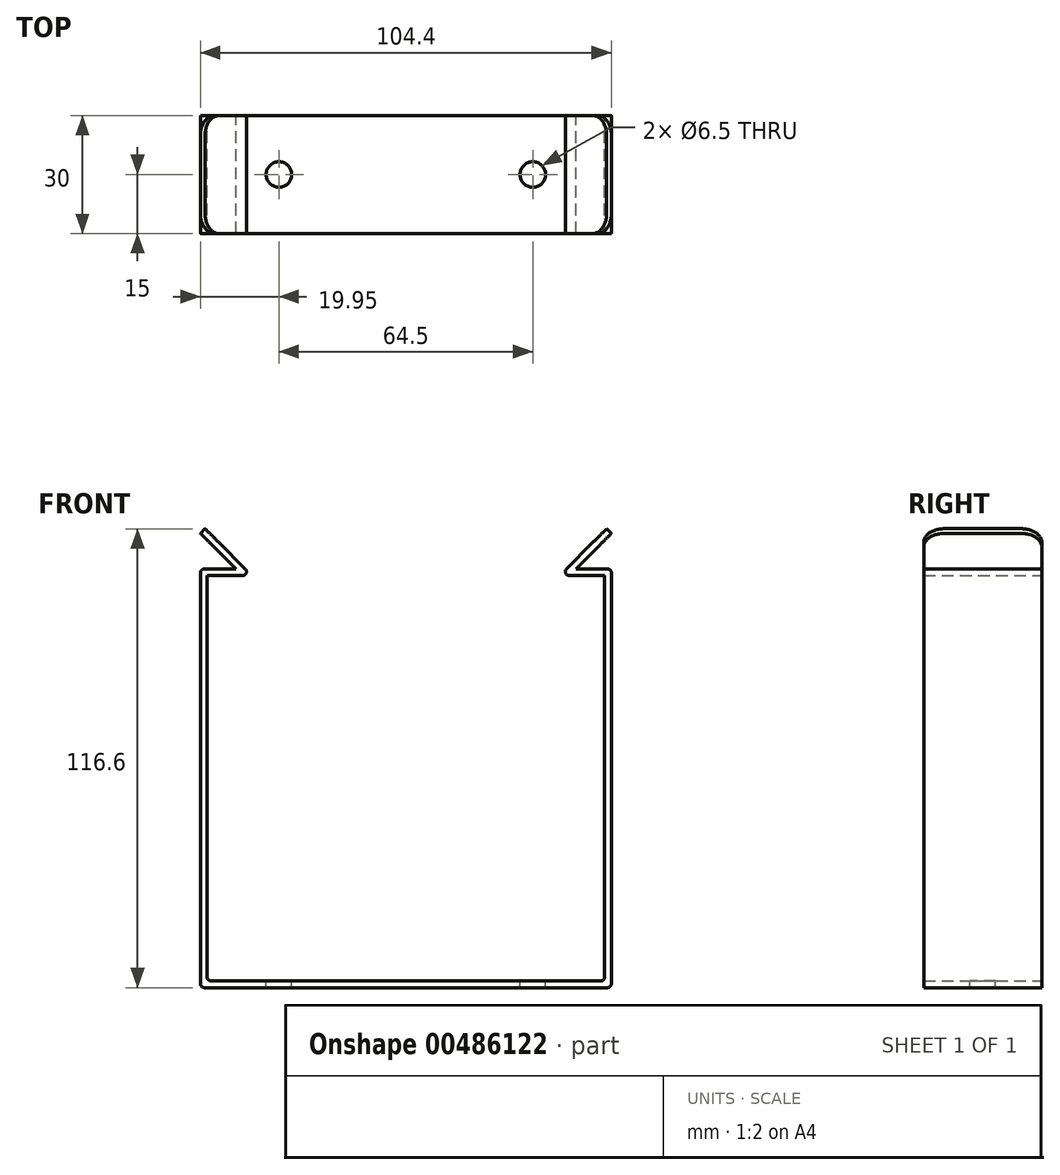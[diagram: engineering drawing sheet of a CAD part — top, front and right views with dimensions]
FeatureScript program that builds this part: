
annotation { "Feature Type Name" : "Feature", "Feature Type Description" : "" }
export const myFeature = defineFeature(function(context is Context, id is Id, definition is map)
    precondition{}
    {
        {
            var Q0;
            Q0=qCreatedBy(makeId("Front.planeOp"),FACE);
            var sketch = newSketch(context, id + "F0", { "sketchPlane" : qUnion([Q0])});
            skLineSegment(sketch, "E0", {"start": v(0, 0) * mm, "end": v(50.5, 0) * mm});
            skLineSegment(sketch, "E1", {"start": v(50.5, 0) * mm, "end": v(50.5, 103) * mm});
            skLineSegment(sketch, "E2", {"start": v(50.5, 103) * mm, "end": v(41.29, 103) * mm});
            skLineSegment(sketch, "E3", {"start": v(0, -1.7) * mm, "end": v(52.2, -1.7) * mm});
            skLineSegment(sketch, "E4", {"start": v(52.2, -1.7) * mm, "end": v(52.2, 104.7) * mm});
            skLineSegment(sketch, "E5", {"start": v(52.2, 104.7) * mm, "end": v(43.2, 104.7) * mm});
            skLineSegment(sketch, "E6", {"start": v(43.2, 104.7) * mm, "end": v(52.2, 113.7) * mm});
            skLineSegment(sketch, "E7", {"start": v(52.2, 113.7) * mm, "end": v(51, 114.9) * mm});
            skLineSegment(sketch, "E8", {"start": v(51, 114.9) * mm, "end": v(39.1, 103) * mm});
            skLineSegment(sketch, "E9", {"start": v(39.1, 103) * mm, "end": v(41.29, 103) * mm});
            skLineSegment(sketch, "E10.MirrorCS", {"start": v(-52.2, 113.7) * mm, "end": v(-51, 114.9) * mm});
            skLineSegment(sketch, "E11.MirrorCS", {"start": v(-39.1, 103) * mm, "end": v(-41.29, 103) * mm});
            skLineSegment(sketch, "E12.MirrorCS", {"start": v(-50.5, 103) * mm, "end": v(-41.29, 103) * mm});
            skLineSegment(sketch, "E13.MirrorCS", {"start": v(-43.2, 104.7) * mm, "end": v(-52.2, 113.7) * mm});
            skLineSegment(sketch, "E14.MirrorCS", {"start": v(-52.2, 104.7) * mm, "end": v(-43.2, 104.7) * mm});
            skLineSegment(sketch, "E15.MirrorCS", {"start": v(-51, 114.9) * mm, "end": v(-39.1, 103) * mm});
            skLineSegment(sketch, "E16.MirrorCS", {"start": v(0, 0) * mm, "end": v(-50.5, 0) * mm});
            skLineSegment(sketch, "E17.MirrorCS", {"start": v(-50.5, 0) * mm, "end": v(-50.5, 103) * mm});
            skLineSegment(sketch, "E18.MirrorCS", {"start": v(0, -1.7) * mm, "end": v(-52.2, -1.7) * mm});
            skLineSegment(sketch, "E19.MirrorCS", {"start": v(-52.2, -1.7) * mm, "end": v(-52.2, 104.7) * mm});
            skSolve(sketch);
        }
        {
            var Q0;
            Q0=makeQuery(id+"F0.imprint","IMPRINT",FACE,{"disambiguationData":[TD([[makeQuery(id+"F0.imprint","IMPRINT",EDGE,{"derivedFrom":sQuery(id+"F0.wireOp",EDGE,"E0")}),-1.0]])]});
            extrude(context, id + "F1", {"entities" : qUnion([Q0]), "depth" : 30 * mm});
        }
        {
            var Q0;
            Q0=makeQuery(id+"F1.opExtrude","SWEPT_FACE",FACE,{"disambiguationData":[OSD([sQuery(id+"F0.wireOp",EDGE,"E0"),sQuery(id+"F0.wireOp",EDGE,"E16.MirrorCS")])]});
            var sketch = newSketch(context, id + "F2", { "sketchPlane" : qUnion([Q0])});
            skCircle(sketch, "E20", {"center": v(-32.25, -15) * mm, "radius": 3.25 * mm});
            skCircle(sketch, "E21.MirrorC", {"center": v(32.25, -15) * mm, "radius": 3.25 * mm});
            skSolve(sketch);
        }
        {
            var Q0;
            Q0=sQuery(id+"F2.wireOp",VERTEX,"E21.MirrorC.center");
            var Q1;
            Q1=sQuery(id+"F2.wireOp",VERTEX,"E20.center");
            var Q2;
            Q2=makeQuery(id+"F1.opExtrude","SWEPT_BODY",BODY,{"disambiguationData":[OSD([sQuery(id+"F0.wireOp",EDGE,"E0"),sQuery(id+"F0.wireOp",EDGE,"E1"),sQuery(id+"F0.wireOp",EDGE,"E2"),sQuery(id+"F0.wireOp",EDGE,"E3"),sQuery(id+"F0.wireOp",EDGE,"E4"),sQuery(id+"F0.wireOp",EDGE,"E5"),sQuery(id+"F0.wireOp",EDGE,"E6"),sQuery(id+"F0.wireOp",EDGE,"E7"),sQuery(id+"F0.wireOp",EDGE,"E8"),sQuery(id+"F0.wireOp",EDGE,"E9"),sQuery(id+"F0.wireOp",EDGE,"E10.MirrorCS"),sQuery(id+"F0.wireOp",EDGE,"E11.MirrorCS"),sQuery(id+"F0.wireOp",EDGE,"E12.MirrorCS"),sQuery(id+"F0.wireOp",EDGE,"E13.MirrorCS"),sQuery(id+"F0.wireOp",EDGE,"E14.MirrorCS"),sQuery(id+"F0.wireOp",EDGE,"E15.MirrorCS"),sQuery(id+"F0.wireOp",EDGE,"E16.MirrorCS"),sQuery(id+"F0.wireOp",EDGE,"E17.MirrorCS"),sQuery(id+"F0.wireOp",EDGE,"E18.MirrorCS"),sQuery(id+"F0.wireOp",EDGE,"E19.MirrorCS")])]});
            hole(context, id + "F3", {"style" : HoleStyle.SIMPLE, "endStyle" : HoleEndStyle.THROUGH, "holeDiameter" : 6.5 * mm, "isTappedThrough" : true, "tappedDepth" : 12 * mm, "tapClearance" : 3, "locations" : qUnion([Q0, Q1]), "scope" : qUnion([Q2])});
        }
        {
            var Q0;
            Q0=makeQuery(id+"F1.opExtrude","CAP_EDGE",EDGE,{"disambiguationData":[OSD([sQuery(id+"F0.wireOp",EDGE,"E10.MirrorCS")])],"isStart":true});
            var Q1;
            Q1=makeQuery(id+"F1.opExtrude","CAP_EDGE",EDGE,{"disambiguationData":[OSD([sQuery(id+"F0.wireOp",EDGE,"E10.MirrorCS")])],"isStart":false});
            var Q2;
            Q2=makeQuery(id+"F1.opExtrude","CAP_EDGE",EDGE,{"disambiguationData":[OSD([sQuery(id+"F0.wireOp",EDGE,"E7")])],"isStart":true});
            var Q3;
            Q3=makeQuery(id+"F1.opExtrude","CAP_EDGE",EDGE,{"disambiguationData":[OSD([sQuery(id+"F0.wireOp",EDGE,"E7")])],"isStart":false});
            fillet(context, id + "F4", {"entities" : qUnion([Q0, Q1, Q2, Q3]), "radius" : 5 * mm, "tangentPropagation" : true, "allowEdgeOverflow" : false});
        }
        {
            var Q0;
            Q0=makeQuery(id+"F1.opExtrude","SWEPT_EDGE",EDGE,{"disambiguationData":[OSD([sQuery(id+"F0.wireOp",EDGE,"E4"),sQuery(id+"F0.wireOp",EDGE,"E5")])]});
            var Q1;
            Q1=makeQuery(id+"F1.opExtrude","SWEPT_EDGE",EDGE,{"disambiguationData":[OSD([sQuery(id+"F0.wireOp",EDGE,"E11.MirrorCS"),sQuery(id+"F0.wireOp",EDGE,"E15.MirrorCS")])]});
            var Q2;
            Q2=makeQuery(id+"F1.opExtrude","SWEPT_EDGE",EDGE,{"disambiguationData":[OSD([sQuery(id+"F0.wireOp",EDGE,"E14.MirrorCS"),sQuery(id+"F0.wireOp",EDGE,"E19.MirrorCS")])]});
            var Q3;
            Q3=makeQuery(id+"F1.opExtrude","SWEPT_EDGE",EDGE,{"disambiguationData":[OSD([sQuery(id+"F0.wireOp",EDGE,"E16.MirrorCS"),sQuery(id+"F0.wireOp",EDGE,"E17.MirrorCS")])]});
            var Q4;
            Q4=makeQuery(id+"F1.opExtrude","SWEPT_EDGE",EDGE,{"disambiguationData":[OSD([sQuery(id+"F0.wireOp",EDGE,"E3"),sQuery(id+"F0.wireOp",EDGE,"E4")])]});
            var Q5;
            Q5=makeQuery(id+"F1.opExtrude","SWEPT_EDGE",EDGE,{"disambiguationData":[OSD([sQuery(id+"F0.wireOp",EDGE,"E8"),sQuery(id+"F0.wireOp",EDGE,"E9")])]});
            var Q6;
            Q6=makeQuery(id+"F1.opExtrude","SWEPT_EDGE",EDGE,{"disambiguationData":[OSD([sQuery(id+"F0.wireOp",EDGE,"E0"),sQuery(id+"F0.wireOp",EDGE,"E1")])]});
            var Q7;
            Q7=makeQuery(id+"F1.opExtrude","SWEPT_EDGE",EDGE,{"disambiguationData":[OSD([sQuery(id+"F0.wireOp",EDGE,"E18.MirrorCS"),sQuery(id+"F0.wireOp",EDGE,"E19.MirrorCS")])]});
            fillet(context, id + "F5", {"entities" : qUnion([Q0, Q1, Q2, Q3, Q4, Q5, Q6, Q7]), "radius" : 1 * mm, "tangentPropagation" : true, "allowEdgeOverflow" : false});
        }
    });
